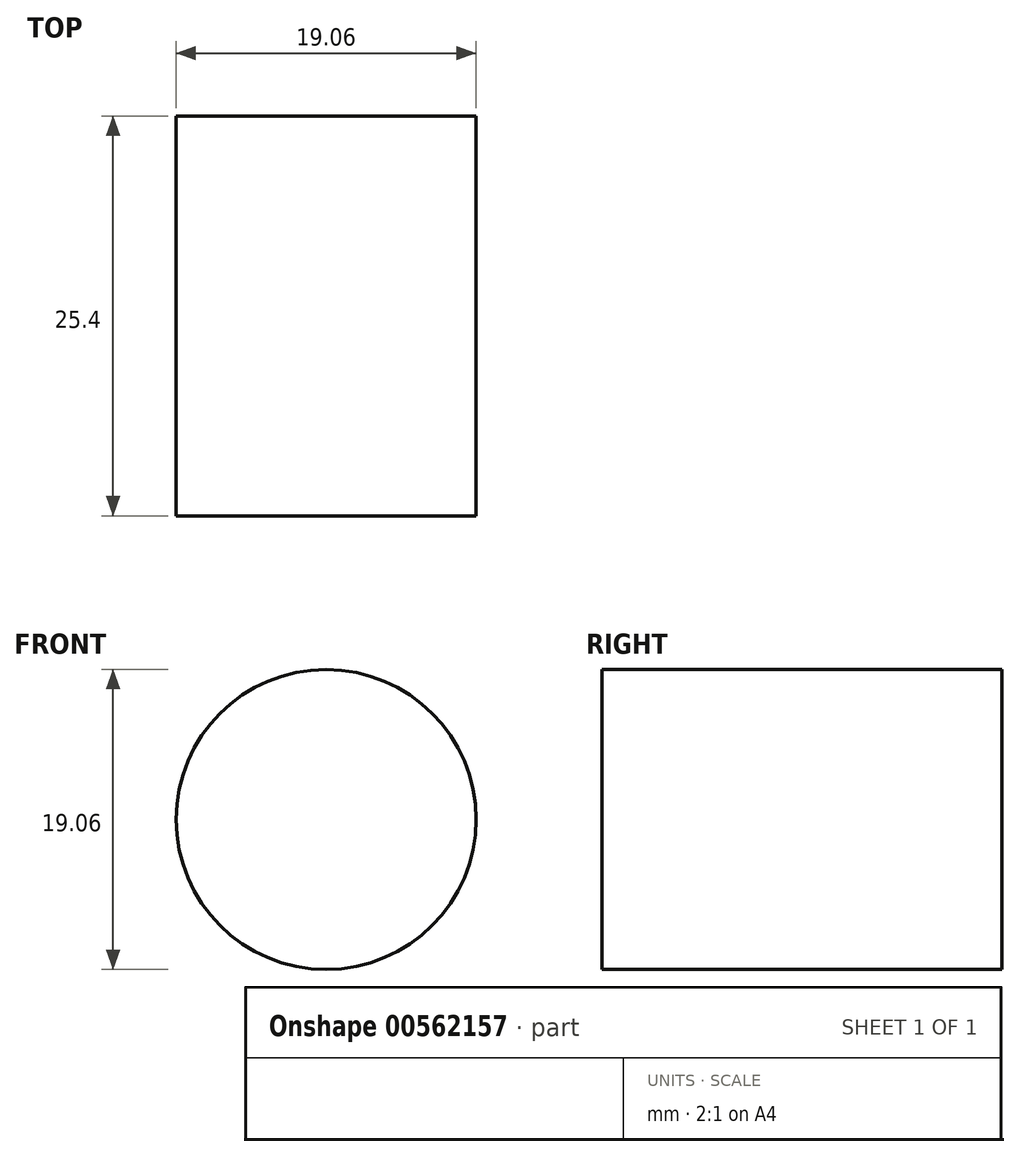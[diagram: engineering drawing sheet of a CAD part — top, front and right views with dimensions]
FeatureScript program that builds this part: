
annotation { "Feature Type Name" : "Feature", "Feature Type Description" : "" }
export const myFeature = defineFeature(function(context is Context, id is Id, definition is map)
    precondition{}
    {
        {
            var Q0;
            Q0=qCreatedBy(makeId("Front.planeOp"),FACE);
            var sketch = newSketch(context, id + "F0", { "sketchPlane" : qUnion([Q0])});
            skCircle(sketch, "E0", {"center": v(0, 0) * mm, "radius": 9.53 * mm});
            skSolve(sketch);
        }
        {
            var Q0;
            Q0 = qSketchRegion(id + "F0", true);
            extrude(context, id + "F1", {"entities" : qUnion([Q0]), "oppositeDirection" : true, "depth" : 25.4 * mm, "offsetDistance" : 25.4 * mm});
        }
    });
